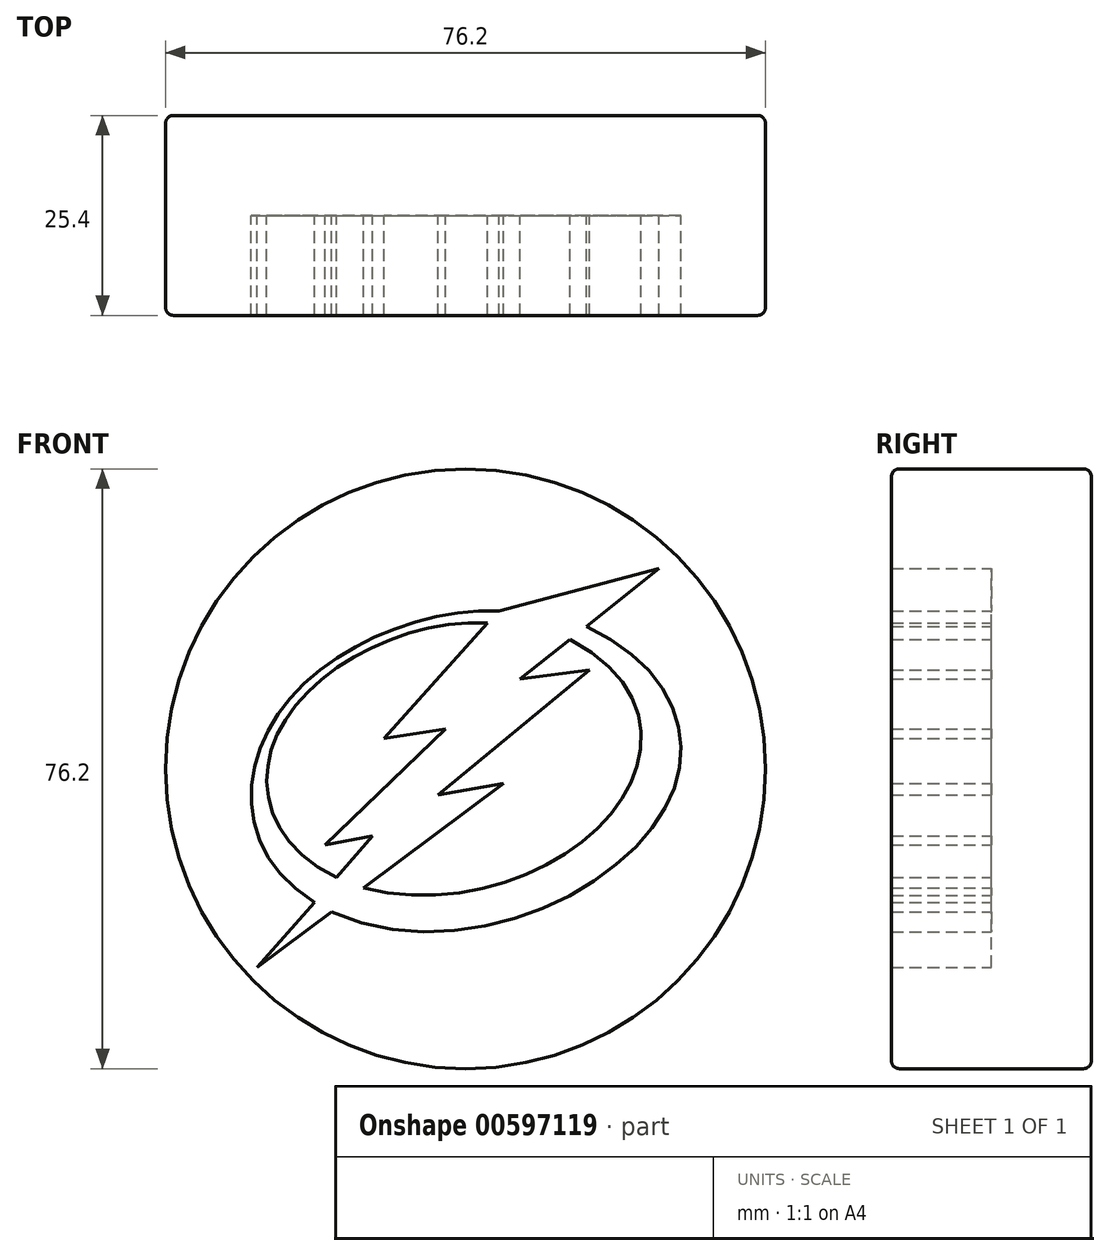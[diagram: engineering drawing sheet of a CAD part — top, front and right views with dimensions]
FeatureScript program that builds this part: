
annotation { "Feature Type Name" : "Feature", "Feature Type Description" : "" }
export const myFeature = defineFeature(function(context is Context, id is Id, definition is map)
    precondition{}
    {
        {
            var Q0;
            Q0=qCreatedBy(makeId("Front.planeOp"),FACE);
            var sketch = newSketch(context, id + "F0", { "sketchPlane" : qUnion([Q0])});
            skLineSegment(sketch, "E0", {"start": v(-26.46, -25.23) * mm, "end": v(4.83, -1.85) * mm});
            skLineSegment(sketch, "E1", {"start": v(4.83, -1.85) * mm, "end": v(-3.5, -3.35) * mm});
            skLineSegment(sketch, "E2", {"start": v(-3.5, -3.35) * mm, "end": v(15.75, 12.56) * mm});
            skLineSegment(sketch, "E3", {"start": v(15.75, 12.56) * mm, "end": v(6.93, 11.42) * mm});
            skLineSegment(sketch, "E4", {"start": v(6.93, 11.42) * mm, "end": v(24.57, 25.42) * mm});
            skLineSegment(sketch, "E5", {"start": v(24.57, 25.42) * mm, "end": v(4.12, 20) * mm});
            skLineSegment(sketch, "E6", {"start": v(-26.46, -25.23) * mm, "end": v(-11.8, -8.54) * mm});
            skLineSegment(sketch, "E7", {"start": v(-11.8, -8.54) * mm, "end": v(-17.82, -9.68) * mm});
            skLineSegment(sketch, "E8", {"start": v(-17.82, -9.68) * mm, "end": v(-2.52, 5.05) * mm});
            skLineSegment(sketch, "E9", {"start": v(-2.52, 5.05) * mm, "end": v(-10.36, 3.83) * mm});
            skLineSegment(sketch, "E10", {"start": v(-10.36, 3.83) * mm, "end": v(4.12, 20) * mm});
            skSolve(sketch);
        }
        {
            var Q0;
            Q0=qCreatedBy(makeId("Front.planeOp"),FACE);
            var sketch = newSketch(context, id + "F1", { "sketchPlane" : qUnion([Q0])});
            skFitSpline(sketch, "E11", {"points": [v(-16.38, -13.8) * mm, v(-23.53, 5.13) * mm, v(2.83, 18.5) * mm], "startDerivative": vector(-59.57, 28.65) * mm, "endDerivative": vector(56, -3.5) * mm});
            skFitSpline(sketch, "E12", {"points": [v(-19.1, -17.02) * mm, v(-24.22, 6.32) * mm, v(4.59, 20.02) * mm], "startDerivative": vector(-61.63, 37.56) * mm, "endDerivative": vector(59.9, -2.9) * mm});
            skLineSegment(sketch, "E13", {"start": v(2.83, 18.5) * mm, "end": v(4.59, 20.02) * mm});
            skLineSegment(sketch, "E14", {"start": v(-16.38, -13.8) * mm, "end": v(-19.1, -17.02) * mm});
            skSolve(sketch);
        }
        {
            var Q0;
            Q0=qCreatedBy(makeId("Front.planeOp"),FACE);
            var sketch = newSketch(context, id + "F2", { "sketchPlane" : qUnion([Q0])});
            skFitSpline(sketch, "E15", {"points": [v(-13.78, -14.93) * mm, v(19.58, -4.23) * mm, v(13.1, 16.5) * mm], "startDerivative": vector(70.95, -19.8) * mm, "endDerivative": vector(-71.21, 36.52) * mm});
            skFitSpline(sketch, "E16", {"points": [v(-17.47, -18.01) * mm, v(25.63, -4.47) * mm, v(14.84, 18.32) * mm], "startDerivative": vector(87.82, -40.05) * mm, "endDerivative": vector(-79, 34.8) * mm});
            skLineSegment(sketch, "E17", {"start": v(-17.47, -18.01) * mm, "end": v(-13.78, -14.93) * mm});
            skLineSegment(sketch, "E18", {"start": v(13.1, 16.5) * mm, "end": v(14.84, 18.32) * mm});
            skSolve(sketch);
        }
        {
            var Q0;
            Q0=qCreatedBy(makeId("Front.planeOp"),FACE);
            var sketch = newSketch(context, id + "F3", { "sketchPlane" : qUnion([Q0])});
            skCircle(sketch, "E19", {"center": v(0, 0) * mm, "radius": 38.1 * mm});
            skSolve(sketch);
        }
        {
            var Q0;
            Q0=makeQuery(id+"F3.imprint","IMPRINT",FACE,{"disambiguationData":[TD([[makeQuery(id+"F3.imprint","IMPRINT",EDGE,{"derivedFrom":sQuery(id+"F3.wireOp",EDGE,"E19")}),1.0]])]});
            extrude(context, id + "F4", {"entities" : qUnion([Q0]), "endBound" : BoundingType.SYMMETRIC, "depth" : 25.4 * mm, "offsetDistance" : 25 * mm});
        }
        {
            var Q0;
            Q0=qSketchRegion(id+"F0",true);
            var Q1;
            Q1=qSketchRegion(id+"F1",true);
            var Q2;
            Q2=qSketchRegion(id+"F2",true);
            extrude(context, id + "F5", {"entities" : qUnion([Q0, Q1, Q2]), "operationType" : NewBodyOperationType.REMOVE, "depth" : 12.7 * mm, "offsetDistance" : 25 * mm});
        }
        {
            var Q0;
            Q0=makeQuery(id+"F4.opExtrude","CAP_EDGE",EDGE,{"disambiguationData":[OSD([sQuery(id+"F3.wireOp",EDGE,"E19")])],"isStart":false});
            var Q1;
            Q1=makeQuery(id+"F4.opExtrude","CAP_EDGE",EDGE,{"disambiguationData":[OSD([sQuery(id+"F3.wireOp",EDGE,"E19")])],"isStart":true});
            fillet(context, id + "F6", {"entities" : qUnion([Q0, Q1]), "radius" : 1 * mm, "tangentPropagation" : true, "allowEdgeOverflow" : false});
        }
    });
